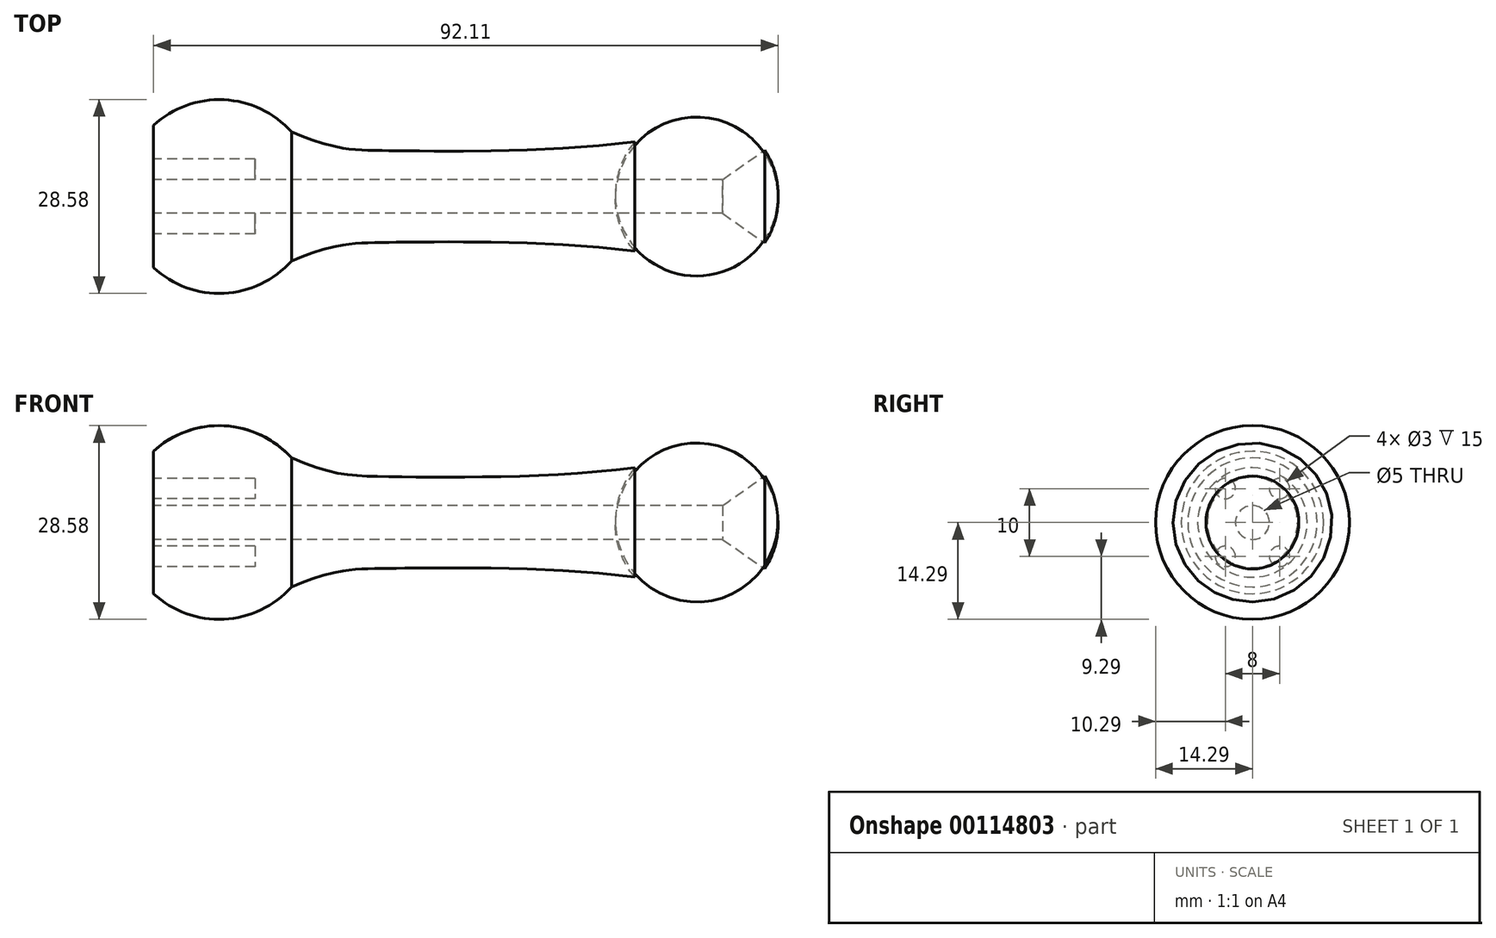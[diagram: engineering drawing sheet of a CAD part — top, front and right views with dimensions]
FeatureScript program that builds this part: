
annotation { "Feature Type Name" : "Feature", "Feature Type Description" : "" }
export const myFeature = defineFeature(function(context is Context, id is Id, definition is map)
    precondition{}
    {
        {
            var Q0;
            Q0=qCreatedBy(makeId("Front.planeOp"),FACE);
            var sketch = newSketch(context, id + "F0", { "sketchPlane" : qUnion([Q0])});
            skLineSegment(sketch, "E0", {"start": v(12.5, 0) * mm, "end": v(57.5, 0) * mm});
            skFitSpline(sketch, "E1", {"points": [v(10.65, 9.52) * mm, v(24.8, 6.77) * mm, v(61.3, 8.08) * mm], "startDerivative": vector(49.03, -20.8) * mm, "endDerivative": vector(62.99, 8.12) * mm});
            skLineSegment(sketch, "E2", {"start": v(12.25, 2.5) * mm, "end": v(74.25, 2.5) * mm});
            skLineSegment(sketch, "E3", {"start": v(74.25, 2.5) * mm, "end": v(80.46, 6.85) * mm});
            skArc(sketch, "E4.trimOffspring", {"start": v(80.46, 6.85) * mm, "mid": v(71.19, 12.25) * mm, "end": v(61.3, 8.08) * mm});
            skPoint(sketch, "E5.end.orphan", {"position": v(82.25, 2.5) * mm});
            skPoint(sketch, "E6.orphan", {"position": v(82.5, 0) * mm});
            skArc(sketch, "E7", {"start": v(10.65, 9.52) * mm, "mid": v(0.69, 14.27) * mm, "end": v(-9.69, 10.5) * mm});
            skLineSegment(sketch, "E8", {"start": v(-9.69, 10.5) * mm, "end": v(-9.69, 2.5) * mm});
            skLineSegment(sketch, "E9", {"start": v(12.25, 2.5) * mm, "end": v(-9.69, 2.5) * mm});
            skSolve(sketch);
        }
        {
            var Q0;
            Q0=makeQuery(id+"F0.imprint","IMPRINT",FACE,{"disambiguationData":[TD([[makeQuery(id+"F0.imprint","IMPRINT",EDGE,{"derivedFrom":sQuery(id+"F0.wireOp",EDGE,"E1")}),-1.0]])]});
            var Q1;
            Q1=sQuery(id+"F0.wireOp",EDGE,"E0");
            revolve(context, id + "F1", {"entities" : qUnion([Q0]), "axis" : qUnion([Q1]), "revolveType" : RevolveType.FULL});
        }
        {
            var Q0;
            Q0=makeQuery(id+"F1.opRevolve","SWEPT_FACE",FACE,{"disambiguationData":[OSD([sQuery(id+"F0.wireOp",EDGE,"E8")])]});
            var sketch = newSketch(context, id + "F2", { "sketchPlane" : qUnion([Q0])});
            skPoint(sketch, "E10.middle", {"position": v(0, 0) * mm});
            skCircle(sketch, "E11", {"center": v(-4, 5) * mm, "radius": 1.5 * mm});
            skCircle(sketch, "E12", {"center": v(4, 5) * mm, "radius": 1.5 * mm});
            skCircle(sketch, "E13", {"center": v(4, -5) * mm, "radius": 1.5 * mm});
            skCircle(sketch, "E14", {"center": v(-4, -5) * mm, "radius": 1.5 * mm});
            skSolve(sketch);
        }
        {
            var Q0;
            Q0 = qSketchRegion(id + "F2", true);
            extrude(context, id + "F3", {"entities" : qUnion([Q0]), "operationType" : NewBodyOperationType.REMOVE, "oppositeDirection" : true, "depth" : 15 * mm});
        }
    });
